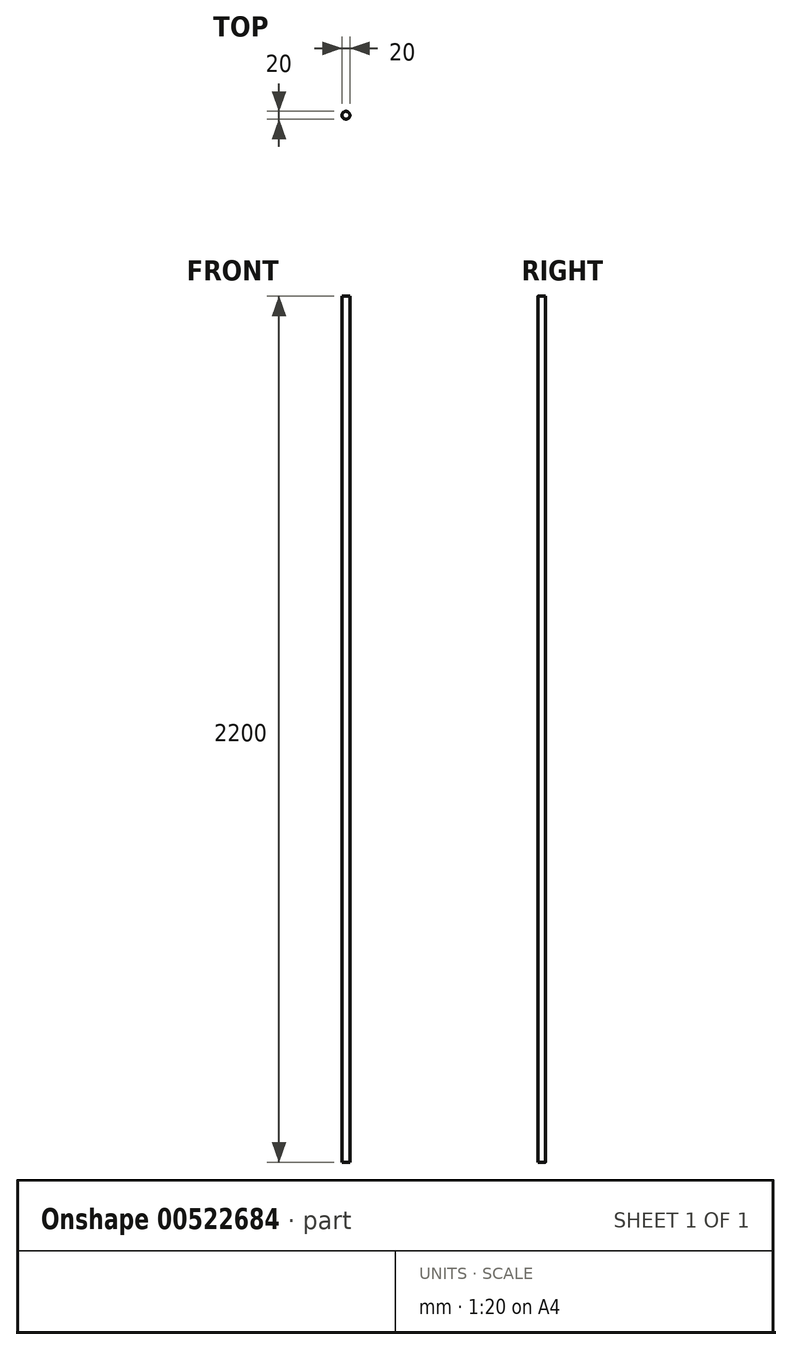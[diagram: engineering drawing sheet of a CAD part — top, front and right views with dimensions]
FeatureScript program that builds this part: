
annotation { "Feature Type Name" : "Feature", "Feature Type Description" : "" }
export const myFeature = defineFeature(function(context is Context, id is Id, definition is map)
    precondition{}
    {
        {
            var Q0;
            Q0=qCreatedBy(makeId("Top.planeOp"),FACE);
            var sketch = newSketch(context, id + "F0", { "sketchPlane" : qUnion([Q0])});
            skCircle(sketch, "E0", {"center": v(0, 0) * mm, "radius": 10 * mm});
            skSolve(sketch);
        }
        {
            var Q0;
            Q0 = qSketchRegion(id + "F0", true);
            extrude(context, id + "F1", {"entities" : qUnion([Q0]), "depth" : 2200 * mm, "offsetDistance" : 25 * mm});
        }
    });
